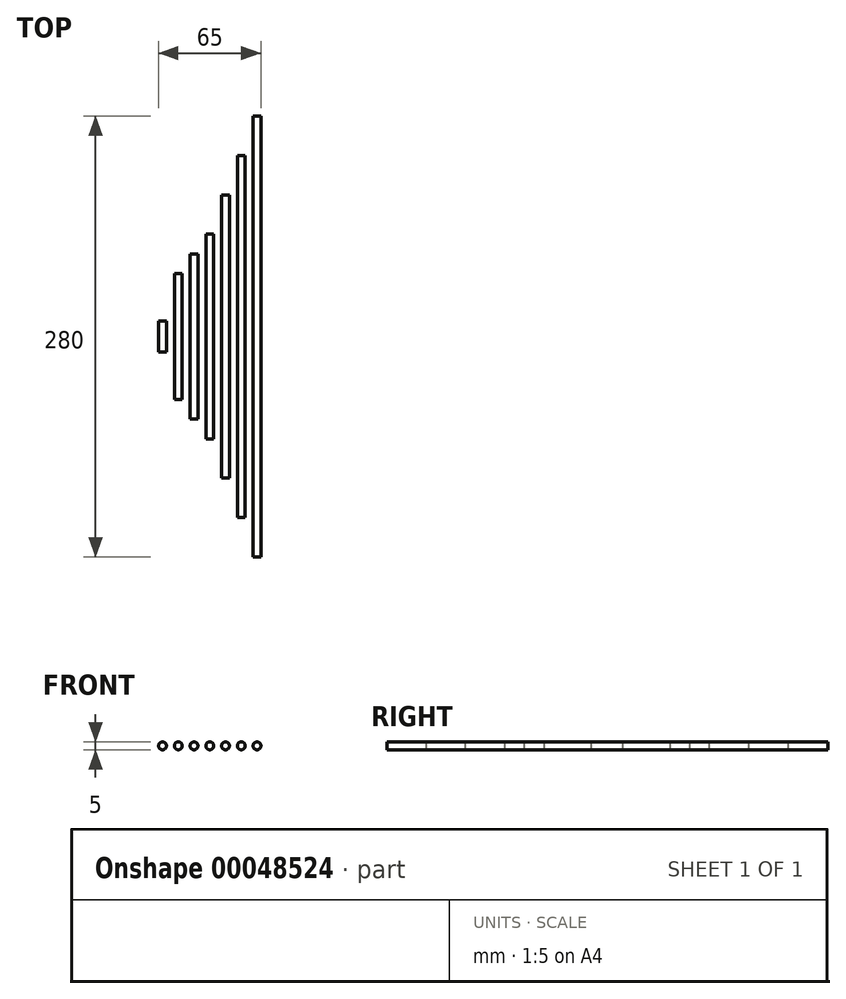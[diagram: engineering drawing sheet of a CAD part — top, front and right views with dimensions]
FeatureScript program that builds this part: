
annotation { "Feature Type Name" : "Feature", "Feature Type Description" : "" }
export const myFeature = defineFeature(function(context is Context, id is Id, definition is map)
    precondition{}
    {
        {
            var Q0;
            Q0=qCreatedBy(makeId("Front.planeOp"),FACE);
            var sketch = newSketch(context, id + "F0", { "sketchPlane" : qUnion([Q0])});
            skLineSegment(sketch, "E0", {"start": v(-30, 0) * mm, "end": v(-20, 0) * mm, "construction": true});
            skLineSegment(sketch, "E1", {"start": v(-20, 0) * mm, "end": v(-10, 0) * mm, "construction": true});
            skLineSegment(sketch, "E2", {"start": v(-10, 0) * mm, "end": v(0, 0) * mm, "construction": true});
            skLineSegment(sketch, "E3", {"start": v(0, 0) * mm, "end": v(10, 0) * mm, "construction": true});
            skLineSegment(sketch, "E4", {"start": v(10, 0) * mm, "end": v(20, 0) * mm, "construction": true});
            skLineSegment(sketch, "E5", {"start": v(20, 0) * mm, "end": v(30, 0) * mm, "construction": true});
            skCircle(sketch, "E6", {"center": v(-30, 0) * mm, "radius": 2.5 * mm});
            skCircle(sketch, "E7", {"center": v(-20, 0) * mm, "radius": 2.5 * mm});
            skCircle(sketch, "E8", {"center": v(-10, 0) * mm, "radius": 2.5 * mm});
            skCircle(sketch, "E9", {"center": v(0, 0) * mm, "radius": 2.5 * mm});
            skCircle(sketch, "E10", {"center": v(10, 0) * mm, "radius": 2.5 * mm});
            skCircle(sketch, "E11", {"center": v(20, 0) * mm, "radius": 2.5 * mm});
            skCircle(sketch, "E12", {"center": v(30, 0) * mm, "radius": 2.5 * mm});
            skSolve(sketch);
        }
        {
            var Q0;
            Q0=makeQuery(id+"F0.imprint","IMPRINT",FACE,{"disambiguationData":[TD([[makeQuery(id+"F0.imprint","IMPRINT",EDGE,{"derivedFrom":sQuery(id+"F0.wireOp",EDGE,"E6")}),1.0]])]});
            extrude(context, id + "F1", {"entities" : qUnion([Q0]), "endBound" : BoundingType.SYMMETRIC, "depth" : 20 * mm});
        }
        {
            var Q0;
            Q0=makeQuery(id+"F0.imprint","IMPRINT",FACE,{"disambiguationData":[TD([[makeQuery(id+"F0.imprint","IMPRINT",EDGE,{"derivedFrom":sQuery(id+"F0.wireOp",EDGE,"E7")}),1.0]])]});
            extrude(context, id + "F2", {"entities" : qUnion([Q0]), "endBound" : BoundingType.SYMMETRIC, "depth" : 80 * mm});
        }
        {
            var Q0;
            Q0=makeQuery(id+"F0.imprint","IMPRINT",FACE,{"disambiguationData":[TD([[makeQuery(id+"F0.imprint","IMPRINT",EDGE,{"derivedFrom":sQuery(id+"F0.wireOp",EDGE,"E8")}),1.0]])]});
            extrude(context, id + "F3", {"entities" : qUnion([Q0]), "endBound" : BoundingType.SYMMETRIC, "depth" : 105 * mm});
        }
        {
            var Q0;
            Q0=makeQuery(id+"F0.imprint","IMPRINT",FACE,{"disambiguationData":[TD([[makeQuery(id+"F0.imprint","IMPRINT",EDGE,{"derivedFrom":sQuery(id+"F0.wireOp",EDGE,"E9")}),1.0]])]});
            extrude(context, id + "F4", {"entities" : qUnion([Q0]), "endBound" : BoundingType.SYMMETRIC, "depth" : 130 * mm});
        }
        {
            var Q0;
            Q0=makeQuery(id+"F0.imprint","IMPRINT",FACE,{"disambiguationData":[TD([[makeQuery(id+"F0.imprint","IMPRINT",EDGE,{"derivedFrom":sQuery(id+"F0.wireOp",EDGE,"E10")}),1.0]])]});
            var Q1;
            Q1=sQuery(id+"F0.wireOp",EDGE,"E10");
            extrude(context, id + "F5", {"entities" : qUnion([Q0]), "surfaceEntities" : qUnion([Q1]), "endBound" : BoundingType.SYMMETRIC, "depth" : 180 * mm});
        }
        {
            var Q0;
            Q0=makeQuery(id+"F0.imprint","IMPRINT",FACE,{"disambiguationData":[TD([[makeQuery(id+"F0.imprint","IMPRINT",EDGE,{"derivedFrom":sQuery(id+"F0.wireOp",EDGE,"E11")}),1.0]])]});
            extrude(context, id + "F6", {"entities" : qUnion([Q0]), "endBound" : BoundingType.SYMMETRIC, "depth" : 230 * mm});
        }
        {
            var Q0;
            Q0=makeQuery(id+"F0.imprint","IMPRINT",FACE,{"disambiguationData":[TD([[makeQuery(id+"F0.imprint","IMPRINT",EDGE,{"derivedFrom":sQuery(id+"F0.wireOp",EDGE,"E12")}),1.0]])]});
            extrude(context, id + "F7", {"entities" : qUnion([Q0]), "endBound" : BoundingType.SYMMETRIC, "depth" : 280 * mm});
        }
    });
